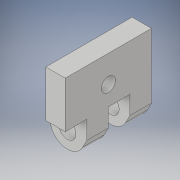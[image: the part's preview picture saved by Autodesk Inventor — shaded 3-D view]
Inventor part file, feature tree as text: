
AUTODESK INVENTOR PART (.ipt)
format: ipt  version: 2018 (Build 220112000, 112)  size: 150,528 bytes
history: native  units: mm
features: sketch x3, extrude x2, projected_geometry x2, hole x1
ambient origin geometry x8: Origin, YZ Plane, XZ Plane, XY Plane, X Axis, Y Axis, Z Axis, Center Point
bodies: Volumenkörper1 (feature_tree)
feature tree (8):
  extrude  "Extrusion1"  Depth=0.8mm
  extrude  "Extrusion2"  Depth=3.0mm
  hole  "Bohrung2"  [1 undecoded]
  sketch  "Skizze1"  dims[d0=0.9mm d2=0.8mm]
  sketch  "Skizze2"  dims[d3=1.6mm d4=3.0mm]
  projected_geometry  "Projizierte Kontur1"
  sketch  "Skizze4"  dims[d5=4.0mm d6=0.0mm d7=0.85mm d8=2.0mm d9=1.0mm d10=1.0mm d11=1.0mm d12=4.0mm d13=0.0mm d22=1.25mm d23=0.65mm d24=6.0mm d25=1.0mm d26=2.0mm d27=90.0deg d28=8.0mm d29=20.594885mm]
  projected_geometry  "Projizierte Kontur3"
note: 1 required parameter value undecoded (feature->parameter linkage not recoverable at this tier; creation-order binding heuristic only, values carry confidence <= 0.55)
